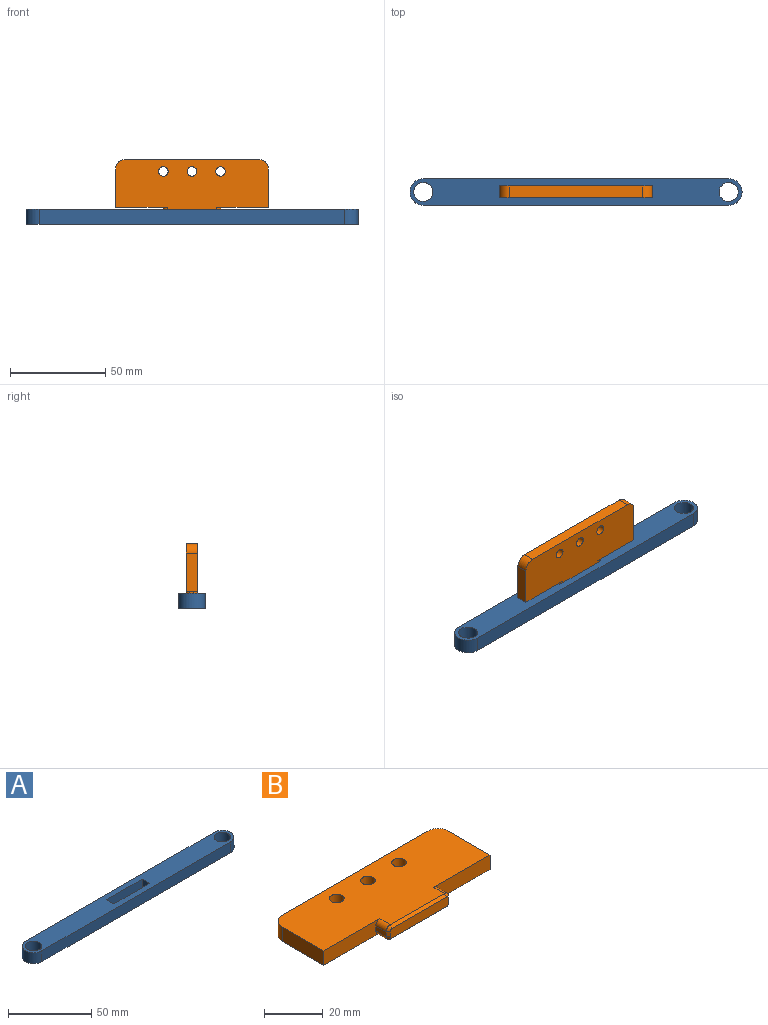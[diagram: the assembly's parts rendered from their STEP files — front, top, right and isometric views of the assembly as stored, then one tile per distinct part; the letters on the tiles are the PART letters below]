
ASSEMBLY  parts=2 mates=1
PART A: 12 faces, bbox 174x14x8 mm
  f0: plane 160x8mm, normal (0,1,0), area 1280mm2, adj f8,f9,f10,f11
  f1: plane 160x8mm, normal (0,-1,0), area 1280mm2, adj f8,f9,f10,f11
  f2: plane 8x6.2mm, normal (1,0,0), area 49.6mm2, adj f3,f5,f8,f9
  f3: plane 30.2x8mm, normal (0,-1,0), area 241.6mm2, adj f2,f4,f8,f9
  f4: plane 8x6.2mm, normal (-1,0,0), area 49.6mm2, adj f3,f5,f8,f9
  f5: plane 30.2x8mm, normal (0,1,0), area 241.6mm2, adj f2,f4,f8,f9
  f6: cylinder r=5mm len=10mm, axis (0,0,-1), area 251.3mm2, adj f8,f9
  f7: cylinder r=5mm len=10mm, axis (0,0,-1), area 251.3mm2, adj f8,f9
  f8: plane 174x14mm, normal (0,0,1), area 2049.6mm2, adj f0,f1,f2,f3,f4,f5,f6,f7
  f9: plane 174x14mm, normal (0,0,-1), area 2049.6mm2, adj f0,f1,f2,f3,f4,f5,f6,f7
  f10: cylinder r=7mm len=14mm, axis (0,0,-1), area 175.9mm2, adj f0,f1,f8,f9
  f11: cylinder r=7mm len=14mm, axis (0,0,-1), area 175.9mm2, adj f0,f1,f8,f9
PART B: 27 faces, bbox 80x31x6 mm
  f0: plane 27x6mm, normal (0,-1,0), area 151.7mm2, adj f7,f8,f9,f10,f15,f17
  f1: plane 27x6mm, normal (0,-1,0), area 151.7mm2, adj f2,f8,f9,f12,f16,f18
  f2: plane 20x6mm, normal (1,0,0), area 120mm2, adj f1,f8,f9,f13
  f3: plane 70x6mm, normal (0,1,0), area 420mm2, adj f8,f9,f13,f14
  f4: cylinder r=2.5mm len=6mm, axis (0,0,-1), area 94.2mm2, adj f8,f9
  f5: cylinder r=2.5mm len=6mm, axis (0,0,-1), area 94.2mm2, adj f8,f9
  f6: cylinder r=2.5mm len=6mm, axis (0,0,-1), area 94.2mm2, adj f8,f9
  f7: plane 20x6mm, normal (-1,0,0), area 120mm2, adj f0,f8,f9,f14
  f8: plane 80x30mm, normal (0,0,1), area 2060.4mm2, adj f0,f1,f2,f3,f4,f5,f6,f7
  f9: plane 80x30mm, normal (0,0,-1), area 2060.4mm2, adj f0,f1,f2,f3,f4,f5,f6,f7
  f10: plane 5x2mm, normal (-1,0,0), area 10mm2, adj f0,f15,f17,f20
  f11: plane 28x4mm, normal (0,-1,0), area 111.1mm2, adj f19,f20,f21,f22,f23,f24,f25,f26
  f12: plane 5x2mm, normal (1,0,0), area 10mm2, adj f1,f16,f18,f25
  f13: cylinder r=5mm len=6mm, axis (0,0,-1), area 47.1mm2, adj f2,f3,f8,f9
  f14: cylinder r=5mm len=6mm, axis (0,0,1), area 47.1mm2, adj f3,f7,f8,f9
  f15: cylinder r=2mm len=5mm, axis (0,-1,0), area 15.7mm2, adj f0,f9,f10,f22
  f16: cylinder r=2mm len=5mm, axis (0,1,0), area 15.7mm2, adj f1,f9,f12,f26
  f17: cylinder r=2mm len=5mm, axis (0,1,0), area 15.7mm2, adj f0,f8,f10,f19
  f18: cylinder r=2mm len=5mm, axis (0,-1,0), area 15.7mm2, adj f1,f8,f12,f23
  f19: cone r=1mm half-angle=45deg, axis (0,1,0), area 3.3mm2, adj f11,f17,f20,f21
  f20: plane 2x1mm, normal (-0.71,-0.71,0), area 2.8mm2, adj f10,f11,f19,f22
  f21: plane 26x1mm, normal (0,-0.71,0.71), area 36.8mm2, adj f8,f11,f19,f23
  f22: cone r=1mm half-angle=45deg, axis (0,1,0), area 3.3mm2, adj f11,f15,f20,f24
  f23: cone r=1mm half-angle=45deg, axis (0,1,0), area 3.3mm2, adj f11,f18,f21,f25
  f24: plane 26x1mm, normal (0,-0.71,-0.71), area 36.8mm2, adj f9,f11,f22,f26
  f25: plane 2x1mm, normal (0.71,-0.71,0), area 2.8mm2, adj f11,f12,f23,f26
  f26: cone r=1mm half-angle=45deg, axis (0,1,0), area 3.3mm2, adj f11,f16,f24,f25
PLACE A t=(-0.01,0.01,-3.98)mm
PLACE B rot(axis=(0,0.71,0.71),180deg) t=(-0.01,0.11,5.02)mm
MATE planar B.f8 <-> A.f3  axis (0,1,0) through (-0.01,3.11,0.02)mm
